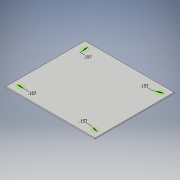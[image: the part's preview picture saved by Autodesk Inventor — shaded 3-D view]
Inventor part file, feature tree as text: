
AUTODESK INVENTOR PART (.ipt)
format: ipt  version: 2018 (Build 220112000, 112)  size: 97,280 bytes
history: native  units: in
note: dims shown in document units (in); Inventor stores cm internally (conversion verified against a paired STEP export)
features: sketch x2, extrude x1
ambient origin geometry x8: Origin, YZ Plane, XZ Plane, XY Plane, X Axis, Y Axis, Z Axis, Center Point
bodies: Solid1 (feature_tree)
feature tree (3):
  extrude  "Extrusion1"  Depth=2.1654in
  sketch  "Sketch2"  dims[d2=0.031in d3=0.0in d4=0.1575in d5=0.1575in d6=0.1575in d7=0.1575in]
  sketch  "Sketch1"  dims[d0=2.4409in d1=2.1654in]
